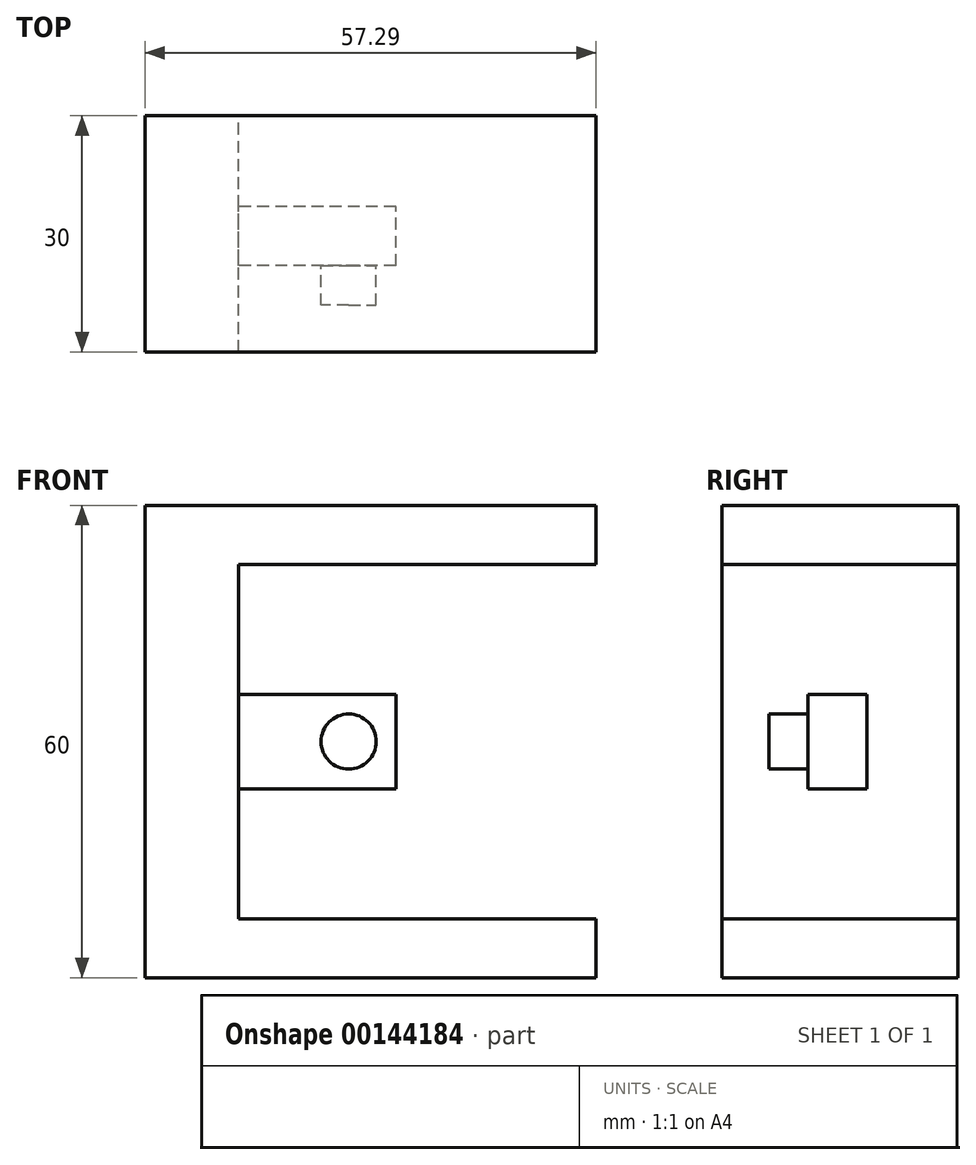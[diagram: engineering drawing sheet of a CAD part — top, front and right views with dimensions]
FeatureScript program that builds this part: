
annotation { "Feature Type Name" : "Feature", "Feature Type Description" : "" }
export const myFeature = defineFeature(function(context is Context, id is Id, definition is map)
    precondition{}
    {
        {
            var Q0;
            Q0=qCreatedBy(makeId("Front.planeOp"),FACE);
            var sketch = newSketch(context, id + "F0", { "sketchPlane" : qUnion([Q0])});
            skLineSegment(sketch, "E0", {"start": v(0, 0) * mm, "end": v(0, 42.71) * mm});
            skLineSegment(sketch, "E1", {"start": v(0, 42.71) * mm, "end": v(57.29, 42.71) * mm});
            skLineSegment(sketch, "E2", {"start": v(57.29, 42.71) * mm, "end": v(57.29, 35.21) * mm});
            skLineSegment(sketch, "E3", {"start": v(57.29, 35.21) * mm, "end": v(11.86, 35.21) * mm});
            skLineSegment(sketch, "E4", {"start": v(11.86, 35.21) * mm, "end": v(11.86, -9.79) * mm});
            skLineSegment(sketch, "E5", {"start": v(11.86, -9.79) * mm, "end": v(57.29, -9.79) * mm});
            skLineSegment(sketch, "E6", {"start": v(57.29, -9.79) * mm, "end": v(57.29, -17.29) * mm});
            skLineSegment(sketch, "E7", {"start": v(57.29, -17.29) * mm, "end": v(0, -17.29) * mm});
            skLineSegment(sketch, "E8", {"start": v(0, -17.29) * mm, "end": v(0, 0) * mm});
            skSolve(sketch);
        }
        {
            var Q0;
            Q0=makeQuery(id+"F0.imprint","IMPRINT",FACE,{"disambiguationData":[TD([[makeQuery(id+"F0.imprint","IMPRINT",EDGE,{"derivedFrom":sQuery(id+"F0.wireOp",EDGE,"E0")}),-1.0]])]});
            extrude(context, id + "F1", {"entities" : qUnion([Q0]), "endBound" : BoundingType.SYMMETRIC, "depth" : 30 * mm});
        }
        {
            var Q0;
            Q0=makeQuery(id+"F1.opExtrude","SWEPT_FACE",FACE,{"disambiguationData":[OSD([sQuery(id+"F0.wireOp",EDGE,"E4")])]});
            var sketch = newSketch(context, id + "F2", { "sketchPlane" : qUnion([Q0])});
            skLineSegment(sketch, "E9.bottom", {"start": v(-4.06, 18.71) * mm, "end": v(3.44, 18.71) * mm});
            skLineSegment(sketch, "E9.top", {"start": v(-4.06, 6.71) * mm, "end": v(3.44, 6.71) * mm});
            skLineSegment(sketch, "E9.left", {"start": v(-4.06, 18.71) * mm, "end": v(-4.06, 6.71) * mm});
            skLineSegment(sketch, "E9.right", {"start": v(3.44, 18.71) * mm, "end": v(3.44, 6.71) * mm});
            skSolve(sketch);
        }
        {
            var Q0;
            Q0=makeQuery(id+"F2.imprint","IMPRINT",FACE,{"disambiguationData":[TD([[makeQuery(id+"F2.imprint","IMPRINT",EDGE,{"derivedFrom":sQuery(id+"F2.wireOp",EDGE,"E9.bottom")}),-1.0]])]});
            extrude(context, id + "F3", {"entities" : qUnion([Q0]), "operationType" : NewBodyOperationType.ADD, "depth" : 20 * mm});
        }
        {
            var Q0;
            Q0=makeQuery(id+"F3.opExtrude","SWEPT_FACE",FACE,{"disambiguationData":[OSD([sQuery(id+"F2.wireOp",EDGE,"E9.left")])]});
            var sketch = newSketch(context, id + "F4", { "sketchPlane" : qUnion([Q0])});
            skCircle(sketch, "E10", {"center": v(25.86, 12.71) * mm, "radius": 3.5 * mm});
            skPoint(sketch, "E10.centerSnap0", {"position": v(31.86, 12.71) * mm});
            skSolve(sketch);
        }
        {
            var Q0;
            Q0=makeQuery(id+"F4.imprint","IMPRINT",FACE,{"disambiguationData":[TD([[makeQuery(id+"F4.imprint","IMPRINT",EDGE,{"derivedFrom":sQuery(id+"F4.wireOp",EDGE,"E10")}),1.0]])]});
            extrude(context, id + "F5", {"entities" : qUnion([Q0]), "operationType" : NewBodyOperationType.ADD, "depth" : 5 * mm});
        }
    });
